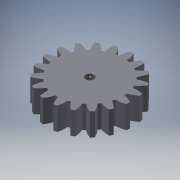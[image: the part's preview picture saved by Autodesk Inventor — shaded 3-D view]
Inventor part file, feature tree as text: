
AUTODESK INVENTOR PART (.ipt)
format: ipt  version: 2016 (Build 200138000, 138)  size: 228,864 bytes
history: native  units: mm (DEFAULTED — no unit token found)
features: sketch x5, plane x3, other x3, extrude x2
ambient origin geometry x8: Origin, YZ Plane, XZ Plane, XY Plane, X Axis, Y Axis, Z Axis, Center Point
bodies: Solid1 (feature_tree)
feature tree (13):
  extrude  "Extrusion1"  Depth=15.0mm TaperAngle=0.0deg
  plane  "Work Plane2"
  plane  "Work Plane8"
  plane  "Work Plane9"
  other  "Spur Gear"
  extrude  "Extrusion2"  Depth=10.0mm TaperAngle=0.0deg
  sketch  "Sketch4"  dims[d17=0.0mm d34=1.65347mm]
  sketch  "Sketch5"  dims[d39=0.0mm d41=0.0mm d43=100.7mm d46=100.7mm d47=0.0mm d48=0.0mm d49=5.5mm d50=10.0mm d51=0.0mm]
  sketch  "Sketch1"  dims[d0=55.65mm d1=15.0mm d2=0.0mm]
  sketch  "Sketch2"  dims[d3=50.35mm d4=10.0mm d5=0.0mm]
  other  "Srf1"
  sketch  "Sketch3"  dims[d16=100.7mm]
  other  "Pitch Diameter"
